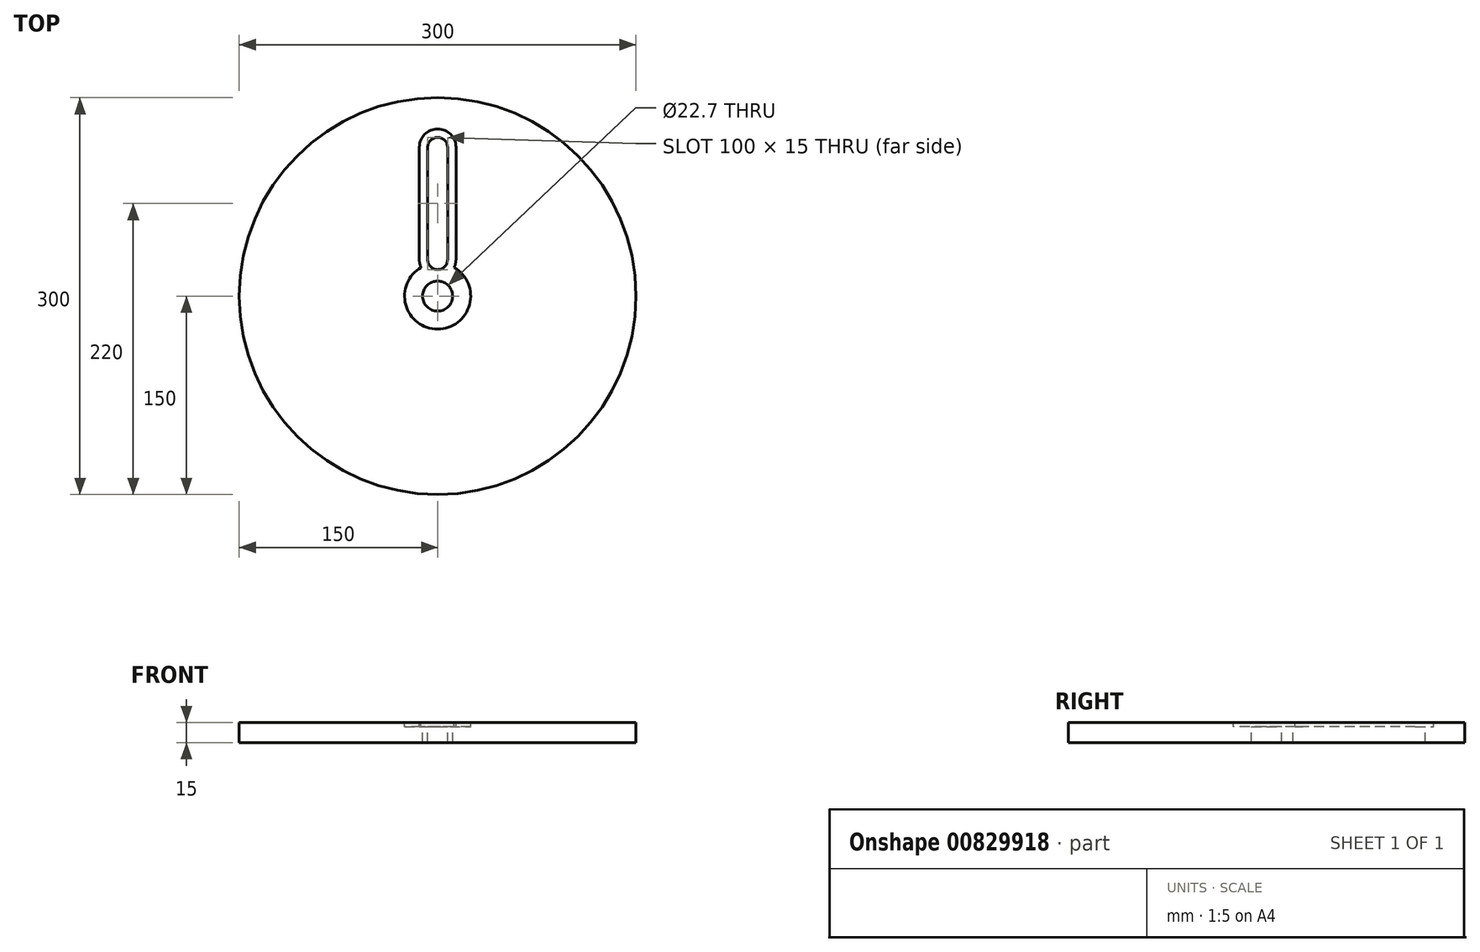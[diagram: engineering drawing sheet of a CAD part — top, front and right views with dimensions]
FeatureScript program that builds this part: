
annotation { "Feature Type Name" : "Feature", "Feature Type Description" : "" }
export const myFeature = defineFeature(function(context is Context, id is Id, definition is map)
    precondition{}
    {
        {
            var Q0;
            Q0=qCreatedBy(makeId("Top.planeOp"),FACE);
            var sketch = newSketch(context, id + "F0", { "sketchPlane" : qUnion([Q0])});
            skCircle(sketch, "E0", {"center": v(0, 0) * mm, "radius": 150 * mm});
            skSolve(sketch);
        }
        {
            var Q0;
            Q0=makeQuery(id+"F0.imprint","IMPRINT",FACE,{"disambiguationData":[TD([[makeQuery(id+"F0.imprint","IMPRINT",EDGE,{"derivedFrom":sQuery(id+"F0.wireOp",EDGE,"E0")}),1.0]])]});
            extrude(context, id + "F1", {"entities" : qUnion([Q0]), "depth" : 15 * mm, "offsetDistance" : 25.4 * mm});
        }
        {
            var Q0;
            Q0=makeQuery(id+"F1.opExtrude","CAP_FACE",FACE,{"disambiguationData":[OSD([sQuery(id+"F0.wireOp",EDGE,"E0")])],"isStart":false});
            var sketch = newSketch(context, id + "F2", { "sketchPlane" : qUnion([Q0])});
            skLineSegment(sketch, "E1.bottom", {"start": v(0, 120) * mm, "end": v(0, 120) * mm});
            skLineSegment(sketch, "E1.top", {"start": v(0, 20) * mm, "end": v(0, 20) * mm});
            skLineSegment(sketch, "E1.left", {"start": v(-7.5, 112.5) * mm, "end": v(-7.5, 27.5) * mm});
            skLineSegment(sketch, "E1.right", {"start": v(0, 120) * mm, "end": v(0, 20) * mm});
            skLineSegment(sketch, "E2.MirrorCS", {"start": v(7.5, 112.5) * mm, "end": v(7.5, 27.5) * mm});
            skPoint(sketch, "E3.visualSharp", {"position": v(-7.5, 120) * mm});
            skArc(sketch, "E3.filletArc", {"start": v(0, 120) * mm, "mid": v(-5.3, 117.8) * mm, "end": v(-7.5, 112.5) * mm});
            skPoint(sketch, "E4.visualSharp", {"position": v(7.5, 120) * mm});
            skArc(sketch, "E4.filletArc", {"start": v(7.5, 112.5) * mm, "mid": v(5.3, 117.8) * mm, "end": v(0, 120) * mm});
            skPoint(sketch, "E5.visualSharp", {"position": v(-7.5, 20) * mm});
            skArc(sketch, "E5.filletArc", {"start": v(-7.5, 27.5) * mm, "mid": v(-5.3, 22.2) * mm, "end": v(0, 20) * mm});
            skPoint(sketch, "E6.visualSharp", {"position": v(7.5, 20) * mm});
            skArc(sketch, "E6.filletArc", {"start": v(0, 20) * mm, "mid": v(5.3, 22.2) * mm, "end": v(7.5, 27.5) * mm});
            skSolve(sketch);
        }
        {
            var Q0;
            Q0=makeQuery(id+"F2.imprint","IMPRINT",FACE,{"disambiguationData":[TD([[makeQuery(id+"F2.imprint","IMPRINT",EDGE,{"derivedFrom":sQuery(id+"F2.wireOp",EDGE,"E1.left")}),1.0]])]});
            var Q1;
            Q1=makeQuery(id+"F2.imprint","IMPRINT",FACE,{"disambiguationData":[TD([[makeQuery(id+"F2.imprint","IMPRINT",EDGE,{"derivedFrom":sQuery(id+"F2.wireOp",EDGE,"E1.right")}),1.0]])]});
            extrude(context, id + "F3", {"entities" : qUnion([Q0, Q1]), "operationType" : NewBodyOperationType.REMOVE, "endBound" : BoundingType.THROUGH_ALL, "oppositeDirection" : true, "depth" : 25.4 * mm, "offsetDistance" : 25.4 * mm});
        }
        {
            var Q0;
            Q0=makeQuery(id+"F1.opExtrude","CAP_FACE",FACE,{"disambiguationData":[OSD([sQuery(id+"F0.wireOp",EDGE,"E0")])],"isStart":false});
            var sketch = newSketch(context, id + "F4", { "sketchPlane" : qUnion([Q0])});
            skArc(sketch, "E7.0", {"start": v(13.85, 112.5) * mm, "mid": v(0, 126.35) * mm, "end": v(-13.85, 112.5) * mm});
            skLineSegment(sketch, "E7.1", {"start": v(13.85, 112.5) * mm, "end": v(13.85, 27.5) * mm});
            skArc(sketch, "E7.2", {"start": v(-13.85, 27.5) * mm, "mid": v(0, 13.65) * mm, "end": v(13.85, 27.5) * mm});
            skLineSegment(sketch, "E7.3", {"start": v(-13.85, 112.5) * mm, "end": v(-13.85, 27.5) * mm});
            skSolve(sketch);
        }
        {
            var Q0;
            Q0=makeQuery(id+"F4.imprint","IMPRINT",FACE,{"disambiguationData":[TD([[makeQuery(id+"F4.imprint","IMPRINT",EDGE,{"derivedFrom":sQuery(id+"F4.wireOp",EDGE,"E7.0")}),1.0]])]});
            extrude(context, id + "F5", {"entities" : qUnion([Q0]), "operationType" : NewBodyOperationType.REMOVE, "oppositeDirection" : true, "depth" : 3 * mm, "offsetDistance" : 25.4 * mm});
        }
        {
            var Q0;
            {var subQ1=sQuery(id+"F4.wireOp",EDGE,"E7.2");var subQ2=sQuery(id+"F4.wireOp",EDGE,"E7.1");var subQ11=makeQuery(id+"F5.boolean.opBoolean","COPY",FACE,{"derivedFrom":makeQuery(id+"F5.opExtrude","SWEPT_FACE",FACE,{"disambiguationData":[OSD([subQ1])]})});var subQ12=makeQuery(id+"F1.opExtrude","CAP_FACE",FACE,{"disambiguationData":[OSD([sQuery(id+"F0.wireOp",EDGE,"E0")])],"isStart":false});var subQ14=makeQuery(id+"FVqTcd0eQH5Maxo_1.1.F5.boolean.opBoolean","COPY",FACE,{"disambiguationData":[TD([makeQuery(id+"FVqTcd0eQH5Maxo_1.1.F5.opExtrude","SWEPT_FACE",FACE,{"disambiguationData":[OSD([subQ2])]})])],"derivedFrom":makeQuery(id+"FVqTcd0eQH5Maxo_1.1.F5.opExtrude","SWEPT_FACE",FACE,{"disambiguationData":[OSD([subQ1])]})});var subQ16=makeQuery(id+"FVqTcd0eQH5Maxo_1.2.F5.boolean.opBoolean","COPY",FACE,{"disambiguationData":[TD([makeQuery(id+"FVqTcd0eQH5Maxo_1.2.F5.opExtrude","SWEPT_FACE",FACE,{"disambiguationData":[OSD([subQ2])]})])],"derivedFrom":makeQuery(id+"FVqTcd0eQH5Maxo_1.2.F5.opExtrude","SWEPT_FACE",FACE,{"disambiguationData":[OSD([subQ1])]})});var subQ18=makeQuery(id+"FVqTcd0eQH5Maxo_1.3.F5.boolean.opBoolean","COPY",FACE,{"disambiguationData":[TD([makeQuery(id+"FVqTcd0eQH5Maxo_1.3.F5.opExtrude","SWEPT_FACE",FACE,{"disambiguationData":[OSD([subQ2])]})])],"derivedFrom":makeQuery(id+"FVqTcd0eQH5Maxo_1.3.F5.opExtrude","SWEPT_FACE",FACE,{"disambiguationData":[OSD([subQ1])]})});Q0=makeQuery(id+"FVqTcd0eQH5Maxo_1.5.F5.boolean.opBoolean","SPLIT",FACE,{"disambiguationData":[TD([subQ11,subQ14,subQ16,subQ18,makeQuery(id+"FVqTcd0eQH5Maxo_1.4.F5.boolean.opBoolean","COPY",FACE,{"disambiguationData":[TD([makeQuery(id+"FVqTcd0eQH5Maxo_1.4.F5.opExtrude","SWEPT_FACE",FACE,{"disambiguationData":[OSD([subQ2])]})])],"derivedFrom":makeQuery(id+"FVqTcd0eQH5Maxo_1.4.F5.opExtrude","SWEPT_FACE",FACE,{"disambiguationData":[OSD([subQ1])]})}),makeQuery(id+"FVqTcd0eQH5Maxo_1.5.F5.opExtrude","SWEPT_FACE",FACE,{"disambiguationData":[OSD([subQ1])]})])],"derivedFrom":subQ12});}
            var sketch = newSketch(context, id + "F6", { "sketchPlane" : qUnion([Q0])});
            skCircle(sketch, "E8", {"center": v(0, 0) * mm, "radius": 25 * mm});
            skCircle(sketch, "E9", {"center": v(0, 0) * mm, "radius": 11.35 * mm});
            skSolve(sketch);
        }
        {
            var Q0;
            Q0=makeQuery(id+"F6.imprint","IMPRINT",FACE,{"disambiguationData":[TD([[makeQuery(id+"F6.imprint","IMPRINT",EDGE,{"derivedFrom":sQuery(id+"F6.wireOp",EDGE,"E8")}),1.0]])]});
            var Q1;
            Q1=makeQuery(id+"F6.imprint","IMPRINT",FACE,{"disambiguationData":[TD([[makeQuery(id+"F6.imprint","IMPRINT",EDGE,{"derivedFrom":sQuery(id+"F6.wireOp",EDGE,"E9")}),1.0]])]});
            var Q2;
            Q2=makeQuery(id+"F6.imprint","IMPRINT",FACE,{"disambiguationData":[TD([[makeQuery(id+"F6.imprint","IMPRINT",EDGE,{"derivedFrom":sQuery(id+"F6.wireOp",EDGE,"E9")}),-1.0]])]});
            var Q3;
            {var subQ0=sQuery(id+"F4.wireOp",EDGE,"E7.3");var subQ1=sQuery(id+"F4.wireOp",EDGE,"E7.2");var subQ2=sQuery(id+"F4.wireOp",EDGE,"E7.1");var subQ3=sQuery(id+"F4.wireOp",EDGE,"E7.0");var subQ4=sQuery(id+"F2.wireOp",EDGE,"E6.filletArc");var subQ5=sQuery(id+"F2.wireOp",EDGE,"E5.filletArc");var subQ6=sQuery(id+"F2.wireOp",EDGE,"E4.filletArc");var subQ7=sQuery(id+"F2.wireOp",EDGE,"E3.filletArc");var subQ8=sQuery(id+"F2.wireOp",EDGE,"E2.MirrorCS");var subQ9=sQuery(id+"F2.wireOp",EDGE,"E1.left");Q3=makeQuery(id+"FVqTcd0eQH5Maxo_1.5.F5.boolean.opBoolean","MERGE",FACE,{"derivedFrom":[makeQuery(id+"FVqTcd0eQH5Maxo_1.4.F5.boolean.opBoolean","MERGE",FACE,{"derivedFrom":[makeQuery(id+"FVqTcd0eQH5Maxo_1.3.F5.boolean.opBoolean","MERGE",FACE,{"derivedFrom":[makeQuery(id+"FVqTcd0eQH5Maxo_1.2.F5.boolean.opBoolean","MERGE",FACE,{"derivedFrom":[makeQuery(id+"FVqTcd0eQH5Maxo_1.1.F5.boolean.opBoolean","MERGE",FACE,{"derivedFrom":[makeQuery(id+"F5.boolean.opBoolean","COPY",FACE,{"derivedFrom":makeQuery(id+"F5.opExtrude","CAP_FACE",FACE,{"disambiguationData":[OSD([subQ9,subQ8,subQ7,subQ6,subQ5,subQ4,subQ3,subQ2,subQ1,subQ0])],"isStart":false})}),makeQuery(id+"FVqTcd0eQH5Maxo_1.1.F5.opExtrude","CAP_FACE",FACE,{"disambiguationData":[OSD([subQ9,subQ8,subQ7,subQ6,subQ5,subQ4,subQ3,subQ2,subQ1,subQ0])],"isStart":false})]}),makeQuery(id+"FVqTcd0eQH5Maxo_1.2.F5.opExtrude","CAP_FACE",FACE,{"disambiguationData":[OSD([subQ9,subQ8,subQ7,subQ6,subQ5,subQ4,subQ3,subQ2,subQ1,subQ0])],"isStart":false})]}),makeQuery(id+"FVqTcd0eQH5Maxo_1.3.F5.opExtrude","CAP_FACE",FACE,{"disambiguationData":[OSD([subQ9,subQ8,subQ7,subQ6,subQ5,subQ4,subQ3,subQ2,subQ1,subQ0])],"isStart":false})]}),makeQuery(id+"FVqTcd0eQH5Maxo_1.4.F5.opExtrude","CAP_FACE",FACE,{"disambiguationData":[OSD([subQ9,subQ8,subQ7,subQ6,subQ5,subQ4,subQ3,subQ2,subQ1,subQ0])],"isStart":false})]}),makeQuery(id+"FVqTcd0eQH5Maxo_1.5.F5.opExtrude","CAP_FACE",FACE,{"disambiguationData":[OSD([subQ9,subQ8,subQ7,subQ6,subQ5,subQ4,subQ3,subQ2,subQ1,subQ0])],"isStart":false})]});}
            extrude(context, id + "F7", {"entities" : qUnion([Q0, Q1, Q2]), "operationType" : NewBodyOperationType.REMOVE, "endBound" : BoundingType.UP_TO_SURFACE, "oppositeDirection" : true, "depth" : 25.4 * mm, "endBoundEntityFace" : qUnion([Q3]), "offsetDistance" : 25.4 * mm});
        }
        {
            var Q0;
            Q0=makeQuery(id+"F6.imprint","IMPRINT",FACE,{"disambiguationData":[TD([[makeQuery(id+"F6.imprint","IMPRINT",EDGE,{"derivedFrom":sQuery(id+"F6.wireOp",EDGE,"E9")}),1.0]])]});
            extrude(context, id + "F8", {"entities" : qUnion([Q0]), "operationType" : NewBodyOperationType.REMOVE, "endBound" : BoundingType.THROUGH_ALL, "oppositeDirection" : true, "depth" : 25.4 * mm, "offsetDistance" : 25.4 * mm});
        }
    });
